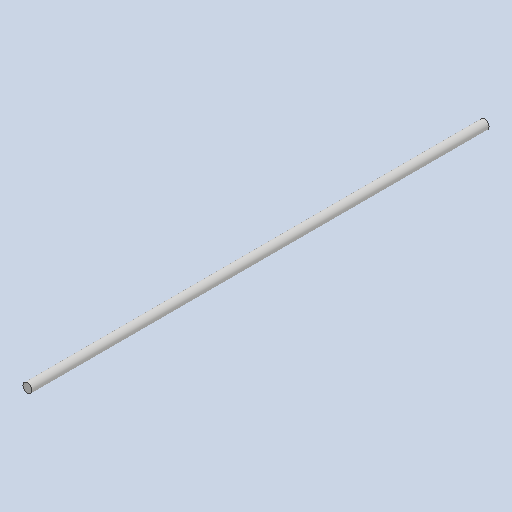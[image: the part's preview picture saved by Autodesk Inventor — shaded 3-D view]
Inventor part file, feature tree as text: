
AUTODESK INVENTOR PART (.ipt)
format: ipt  version: 2023 (Build 270158000, 158)  size: 80,384 bytes
history: native  units: mm
features: extrude x1, sketch x1
ambient origin geometry x8: Origin, YZ Plane, XZ Plane, XY Plane, X Axis, Y Axis, Z Axis, Center Point
bodies: Solid1 (feature_tree)
feature tree (2):
  extrude  "Extrusion1"  Depth=400.0mm
  sketch  "Sketch1"  dims[d0=8.0mm d1=400.0mm d2=0.0mm]
